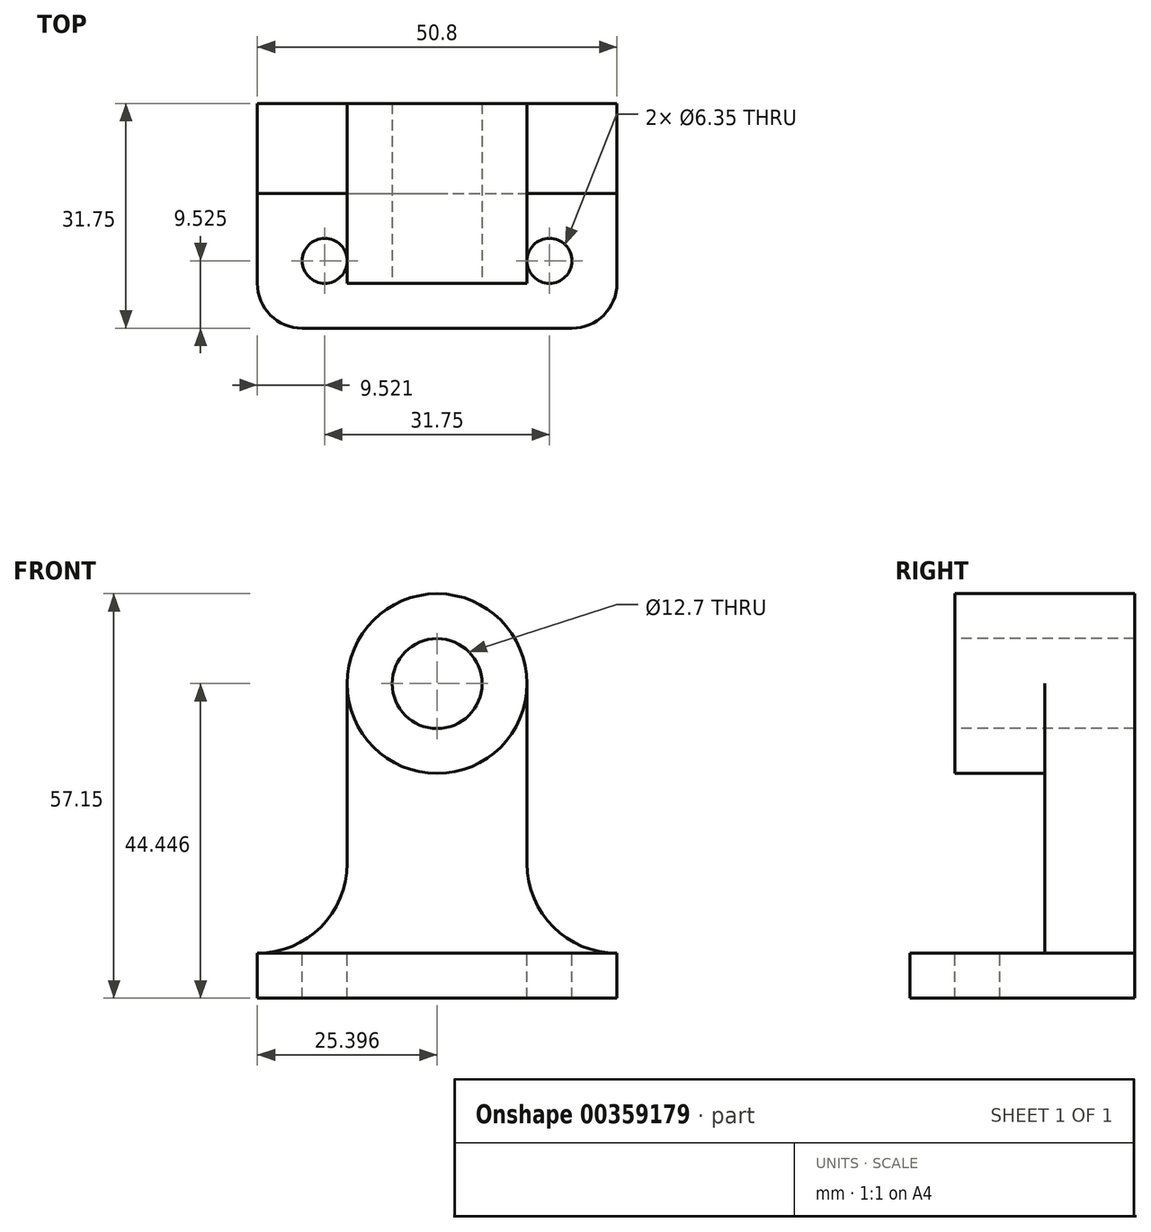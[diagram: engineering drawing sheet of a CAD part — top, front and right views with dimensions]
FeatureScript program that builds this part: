
annotation { "Feature Type Name" : "Feature", "Feature Type Description" : "" }
export const myFeature = defineFeature(function(context is Context, id is Id, definition is map)
    precondition{}
    {
        {
            var Q0;
            Q0=qCreatedBy(makeId("Front.planeOp"),FACE);
            var sketch = newSketch(context, id + "F0", { "sketchPlane" : qUnion([Q0])});
            skLineSegment(sketch, "E0.bottom", {"start": v(-19.36, 20.56) * mm, "end": v(31.44, 20.56) * mm});
            skLineSegment(sketch, "E0.top", {"start": v(-19.36, -36.6) * mm, "end": v(31.44, -36.6) * mm});
            skLineSegment(sketch, "E0.left", {"start": v(-19.36, 20.56) * mm, "end": v(-19.36, -36.6) * mm});
            skLineSegment(sketch, "E0.right", {"start": v(31.44, 20.56) * mm, "end": v(31.44, -36.6) * mm});
            skSolve(sketch);
        }
        {
            var Q0;
            Q0=makeQuery(id+"F0.imprint","IMPRINT",FACE,{"disambiguationData":[TD([[makeQuery(id+"F0.imprint","IMPRINT",EDGE,{"derivedFrom":sQuery(id+"F0.wireOp",EDGE,"E0.bottom")}),-1.0]])]});
            extrude(context, id + "F1", {"entities" : qUnion([Q0]), "depth" : 31.75 * mm});
        }
        {
            var Q0;
            Q0=makeQuery(id+"F1.opExtrude","CAP_FACE",FACE,{"disambiguationData":[OSD([sQuery(id+"F0.wireOp",EDGE,"E0.bottom"),sQuery(id+"F0.wireOp",EDGE,"E0.top"),sQuery(id+"F0.wireOp",EDGE,"E0.left"),sQuery(id+"F0.wireOp",EDGE,"E0.right")])],"isStart":false});
            var sketch = newSketch(context, id + "F2", { "sketchPlane" : qUnion([Q0])});
            skLineSegment(sketch, "E1", {"start": v(-19.36, -30.24) * mm, "end": v(31.44, -30.24) * mm});
            skSolve(sketch);
        }
        {
            var Q0;
            {var subQ0=sQuery(id+"F2.wireOp",EDGE,"E1");Q0=makeQuery(id+"F2.imprint","IMPRINT",FACE,{"disambiguationData":[TD([[makeQuery(id+"F2.imprint","IMPRINT",EDGE,{"derivedFrom":subQ0}),1.0]])]});}
            extrude(context, id + "F3", {"entities" : qUnion([Q0]), "operationType" : NewBodyOperationType.ADD, "depth" : 6.35 * mm});
        }
        {
            var Q0;
            Q0=makeQuery(id+"F3.opExtrude","CAP_FACE",FACE,{"disambiguationData":[OSD([sQuery(id+"F0.wireOp",EDGE,"E0.bottom"),sQuery(id+"F0.wireOp",EDGE,"E0.left"),sQuery(id+"F0.wireOp",EDGE,"E0.right"),sQuery(id+"F2.wireOp",EDGE,"E1")])],"isStart":false});
            extrude(context, id + "F4", {"entities" : qUnion([Q0]), "operationType" : NewBodyOperationType.REMOVE, "oppositeDirection" : true, "depth" : 12.7 * mm});
        }
        {
            var Q0;
            Q0=makeQuery(id+"F4.boolean.opBoolean","COPY",FACE,{"derivedFrom":makeQuery(id+"F4.opExtrude","CAP_FACE",FACE,{"disambiguationData":[OSD([sQuery(id+"F0.wireOp",EDGE,"E0.bottom"),sQuery(id+"F0.wireOp",EDGE,"E0.left"),sQuery(id+"F0.wireOp",EDGE,"E0.right"),sQuery(id+"F2.wireOp",EDGE,"E1")])],"isStart":false})});
            var sketch = newSketch(context, id + "F5", { "sketchPlane" : qUnion([Q0])});
            skLineSegment(sketch, "E2", {"start": v(-6.66, 20.56) * mm, "end": v(-6.66, -17.54) * mm});
            skLineSegment(sketch, "E3", {"start": v(18.74, 20.56) * mm, "end": v(18.74, -17.54) * mm});
            skLineSegment(sketch, "E4", {"start": v(-19.36, -30.24) * mm, "end": v(-19.36, -30.24) * mm});
            skLineSegment(sketch, "E5", {"start": v(31.44, -30.24) * mm, "end": v(31.44, -30.24) * mm});
            skPoint(sketch, "E6.visualSharp", {"position": v(18.74, -30.24) * mm});
            skArc(sketch, "E6.filletArc", {"start": v(18.74, -17.54) * mm, "mid": v(22.46, -26.52) * mm, "end": v(31.44, -30.24) * mm});
            skPoint(sketch, "E7.visualSharp", {"position": v(-6.66, -30.24) * mm});
            skArc(sketch, "E7.filletArc", {"start": v(-19.36, -30.24) * mm, "mid": v(-10.38, -26.52) * mm, "end": v(-6.66, -17.54) * mm});
            skSolve(sketch);
        }
        {
            var Q0;
            {var subQ0=sQuery(id+"F5.wireOp",EDGE,"E2");Q0=makeQuery(id+"F5.imprint","IMPRINT",FACE,{"disambiguationData":[TD([[makeQuery(id+"F5.imprint","IMPRINT",EDGE,{"derivedFrom":subQ0}),-1.0]])]});}
            var Q1;
            {var subQ0=sQuery(id+"F5.wireOp",EDGE,"E3");Q1=makeQuery(id+"F5.imprint","IMPRINT",FACE,{"disambiguationData":[TD([[makeQuery(id+"F5.imprint","IMPRINT",EDGE,{"derivedFrom":subQ0}),1.0]])]});}
            extrude(context, id + "F6", {"entities" : qUnion([Q0, Q1]), "operationType" : NewBodyOperationType.REMOVE, "oppositeDirection" : true, "depth" : 25.4 * mm});
        }
        {
            var Q0;
            Q0=makeQuery(id+"F4.boolean.opBoolean","COPY",FACE,{"derivedFrom":makeQuery(id+"F4.opExtrude","CAP_FACE",FACE,{"disambiguationData":[OSD([sQuery(id+"F0.wireOp",EDGE,"E0.bottom"),sQuery(id+"F0.wireOp",EDGE,"E0.left"),sQuery(id+"F0.wireOp",EDGE,"E0.right"),sQuery(id+"F2.wireOp",EDGE,"E1")])],"isStart":false})});
            var sketch = newSketch(context, id + "F7", { "sketchPlane" : qUnion([Q0])});
            skLineSegment(sketch, "E8", {"start": v(6.04, 20.56) * mm, "end": v(6.04, 20.56) * mm});
            skLineSegment(sketch, "E9", {"start": v(18.74, 7.86) * mm, "end": v(18.74, 7.86) * mm});
            skLineSegment(sketch, "E10", {"start": v(6.04, -4.84) * mm, "end": v(6.04, -4.84) * mm});
            skLineSegment(sketch, "E11", {"start": v(-6.66, 7.86) * mm, "end": v(-6.66, 7.86) * mm});
            skPoint(sketch, "E12.visualSharp", {"position": v(-6.66, 20.56) * mm});
            skArc(sketch, "E12.filletArc", {"start": v(6.04, 20.56) * mm, "mid": v(-2.94, 16.84) * mm, "end": v(-6.66, 7.86) * mm});
            skPoint(sketch, "E13.visualSharp", {"position": v(-6.66, -4.84) * mm});
            skArc(sketch, "E13.filletArc", {"start": v(-6.66, 7.86) * mm, "mid": v(-2.94, -1.12) * mm, "end": v(6.04, -4.84) * mm});
            skPoint(sketch, "E14.visualSharp", {"position": v(18.74, -4.84) * mm});
            skArc(sketch, "E14.filletArc", {"start": v(6.04, -4.84) * mm, "mid": v(15.02, -1.12) * mm, "end": v(18.74, 7.86) * mm});
            skPoint(sketch, "E15.visualSharp", {"position": v(18.74, 20.56) * mm});
            skArc(sketch, "E15.filletArc", {"start": v(18.74, 7.86) * mm, "mid": v(15.02, 16.84) * mm, "end": v(6.04, 20.56) * mm});
            skSolve(sketch);
        }
        {
            var Q0;
            {var subQ2=sQuery(id+"F7.wireOp",EDGE,"E13.filletArc");Q0=makeQuery(id+"F7.imprint","IMPRINT",FACE,{"disambiguationData":[TD([[makeQuery(id+"F7.imprint","IMPRINT",EDGE,{"derivedFrom":subQ2}),-1.0]])]});}
            var Q1;
            {var subQ0=sQuery(id+"F7.wireOp",EDGE,"E15.filletArc");Q1=makeQuery(id+"F7.imprint","IMPRINT",FACE,{"disambiguationData":[TD([[makeQuery(id+"F7.imprint","IMPRINT",EDGE,{"derivedFrom":subQ0}),-1.0]])]});}
            var Q2;
            {var subQ0=sQuery(id+"F7.wireOp",EDGE,"E12.filletArc");Q2=makeQuery(id+"F7.imprint","IMPRINT",FACE,{"disambiguationData":[TD([[makeQuery(id+"F7.imprint","IMPRINT",EDGE,{"derivedFrom":subQ0}),-1.0]])]});}
            extrude(context, id + "F8", {"entities" : qUnion([Q0, Q1, Q2]), "operationType" : NewBodyOperationType.REMOVE, "oppositeDirection" : true, "depth" : 12.7 * mm});
        }
        {
            var Q0;
            Q0=makeQuery(id+"F8.boolean.opBoolean","COPY",FACE,{"derivedFrom":makeQuery(id+"F8.opExtrude","CAP_FACE",FACE,{"disambiguationData":[OSD([sQuery(id+"F0.wireOp",EDGE,"E0.bottom"),sQuery(id+"F5.wireOp",EDGE,"E3"),sQuery(id+"F7.wireOp",EDGE,"E15.filletArc")])],"isStart":false})});
            var Q1;
            Q1=makeQuery(id+"F8.boolean.opBoolean","COPY",FACE,{"derivedFrom":makeQuery(id+"F8.opExtrude","CAP_FACE",FACE,{"disambiguationData":[OSD([sQuery(id+"F0.wireOp",EDGE,"E0.bottom"),sQuery(id+"F5.wireOp",EDGE,"E2"),sQuery(id+"F7.wireOp",EDGE,"E12.filletArc")])],"isStart":false})});
            extrude(context, id + "F9", {"entities" : qUnion([Q0, Q1]), "operationType" : NewBodyOperationType.REMOVE, "oppositeDirection" : true, "depth" : 25.4 * mm});
        }
        {
            var Q0;
            Q0=makeQuery(id+"F4.boolean.opBoolean","COPY",FACE,{"derivedFrom":makeQuery(id+"F4.opExtrude","CAP_FACE",FACE,{"disambiguationData":[OSD([sQuery(id+"F0.wireOp",EDGE,"E0.bottom"),sQuery(id+"F0.wireOp",EDGE,"E0.left"),sQuery(id+"F0.wireOp",EDGE,"E0.right"),sQuery(id+"F2.wireOp",EDGE,"E1")])],"isStart":false})});
            var sketch = newSketch(context, id + "F10", { "sketchPlane" : qUnion([Q0])});
            skCircle(sketch, "E16", {"center": v(6.04, 7.86) * mm, "radius": 6.35 * mm});
            skSolve(sketch);
        }
        {
            var Q0;
            Q0=makeQuery(id+"F10.imprint","IMPRINT",FACE,{"disambiguationData":[TD([[makeQuery(id+"F10.imprint","IMPRINT",EDGE,{"derivedFrom":sQuery(id+"F10.wireOp",EDGE,"E16")}),1.0]])]});
            extrude(context, id + "F11", {"entities" : qUnion([Q0]), "operationType" : NewBodyOperationType.REMOVE, "oppositeDirection" : true, "depth" : 50.8 * mm});
        }
        {
            var Q0;
            {var subQ0=sQuery(id+"F2.wireOp",EDGE,"E1");Q0=makeQuery(id+"F8.boolean.opBoolean","MERGE",FACE,{"derivedFrom":[makeQuery(id+"F4.boolean.opBoolean","COPY",FACE,{"derivedFrom":makeQuery(id+"F4.opExtrude","SWEPT_FACE",FACE,{"disambiguationData":[OSD([subQ0])]})})],"fromTools":[makeQuery(id+"F8.opExtrude","SWEPT_FACE",FACE,{"disambiguationData":[OSD([subQ0])]})]});}
            var sketch = newSketch(context, id + "F12", { "sketchPlane" : qUnion([Q0])});
            skLineSegment(sketch, "E17", {"start": v(-19.36, -12.7) * mm, "end": v(-19.36, -25.4) * mm});
            skLineSegment(sketch, "E18", {"start": v(-13.01, -31.75) * mm, "end": v(25.09, -31.75) * mm});
            skLineSegment(sketch, "E19", {"start": v(31.44, -25.4) * mm, "end": v(31.44, -12.7) * mm});
            skPoint(sketch, "E20.visualSharp", {"position": v(-19.36, -31.75) * mm});
            skArc(sketch, "E20.filletArc", {"start": v(-19.36, -25.4) * mm, "mid": v(-17.5, -29.9) * mm, "end": v(-13.01, -31.75) * mm});
            skPoint(sketch, "E21.visualSharp", {"position": v(31.44, -31.75) * mm});
            skArc(sketch, "E21.filletArc", {"start": v(25.09, -31.75) * mm, "mid": v(29.58, -29.9) * mm, "end": v(31.44, -25.4) * mm});
            skCircle(sketch, "E22", {"center": v(-9.84, -22.23) * mm, "radius": 3.18 * mm});
            skCircle(sketch, "E23", {"center": v(21.91, -22.23) * mm, "radius": 3.18 * mm});
            skSolve(sketch);
        }
        {
            var Q0;
            Q0=makeQuery(id+"F12.imprint","IMPRINT",FACE,{"disambiguationData":[TD([[makeQuery(id+"F12.imprint","IMPRINT",EDGE,{"derivedFrom":sQuery(id+"F12.wireOp",EDGE,"E22")}),1.0]])]});
            var Q1;
            {var subQ0=sQuery(id+"F12.wireOp",EDGE,"E20.filletArc");Q1=makeQuery(id+"F12.imprint","IMPRINT",FACE,{"disambiguationData":[TD([[makeQuery(id+"F12.imprint","IMPRINT",EDGE,{"derivedFrom":subQ0}),-1.0]])]});}
            var Q2;
            Q2=makeQuery(id+"F12.imprint","IMPRINT",FACE,{"disambiguationData":[TD([[makeQuery(id+"F12.imprint","IMPRINT",EDGE,{"derivedFrom":sQuery(id+"F12.wireOp",EDGE,"E23")}),1.0]])]});
            var Q3;
            {var subQ0=sQuery(id+"F12.wireOp",EDGE,"E21.filletArc");Q3=makeQuery(id+"F12.imprint","IMPRINT",FACE,{"disambiguationData":[TD([[makeQuery(id+"F12.imprint","IMPRINT",EDGE,{"derivedFrom":subQ0}),-1.0]])]});}
            extrude(context, id + "F13", {"entities" : qUnion([Q0, Q1, Q2, Q3]), "operationType" : NewBodyOperationType.REMOVE, "oppositeDirection" : true, "depth" : 25.4 * mm});
        }
    });
